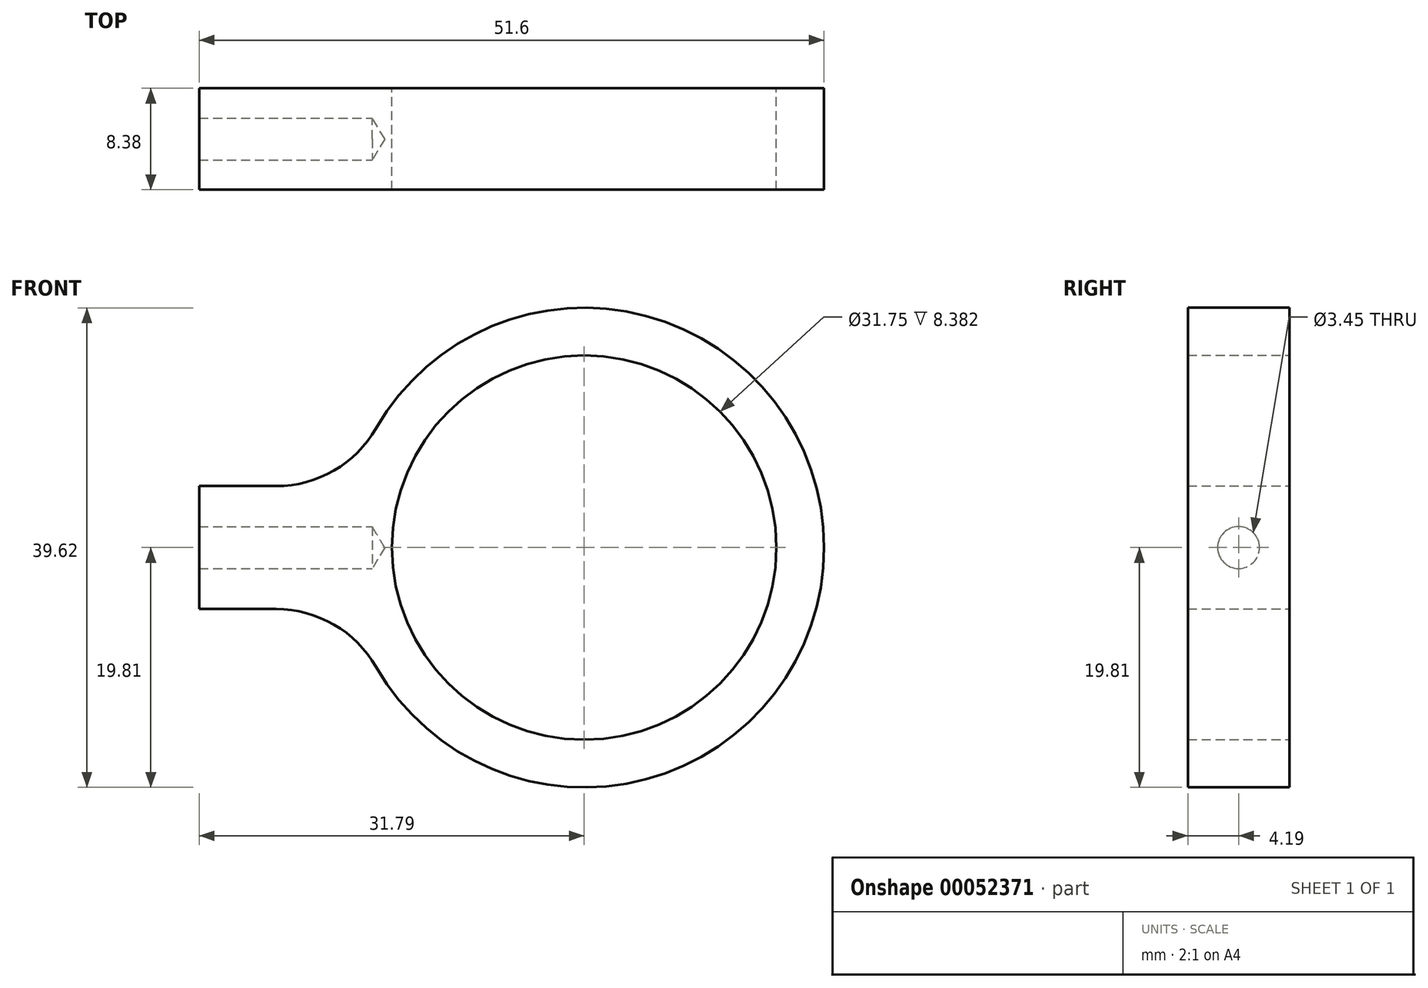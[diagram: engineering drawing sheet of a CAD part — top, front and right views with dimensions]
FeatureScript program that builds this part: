
annotation { "Feature Type Name" : "Feature", "Feature Type Description" : "" }
export const myFeature = defineFeature(function(context is Context, id is Id, definition is map)
    precondition{}
    {
        {
            var Q0;
            Q0=qCreatedBy(makeId("Front.planeOp"),FACE);
            var sketch = newSketch(context, id + "F0", { "sketchPlane" : qUnion([Q0])});
            skCircle(sketch, "E0", {"center": v(0, 0) * mm, "radius": 15.88 * mm});
            skArc(sketch, "E1", {"start": v(-17.18, 9.86) * mm, "mid": v(19.81, 0) * mm, "end": v(-17.18, -9.86) * mm});
            skLineSegment(sketch, "E2", {"start": v(-25.44, -5.08) * mm, "end": v(-31.8, -5.08) * mm});
            skLineSegment(sketch, "E3", {"start": v(-31.8, -5.08) * mm, "end": v(-31.8, 5.08) * mm});
            skLineSegment(sketch, "E4", {"start": v(-31.8, 5.08) * mm, "end": v(-25.44, 5.08) * mm});
            skPoint(sketch, "E5", {"position": v(-31.8, 0) * mm});
            skPoint(sketch, "E6.visualSharp", {"position": v(-19.15, 5.08) * mm});
            skArc(sketch, "E6.filletArc", {"start": v(-25.44, 5.08) * mm, "mid": v(-20.67, 6.36) * mm, "end": v(-17.18, 9.86) * mm});
            skPoint(sketch, "E7.visualSharp", {"position": v(-19.15, -5.08) * mm});
            skArc(sketch, "E7.filletArc", {"start": v(-17.18, -9.86) * mm, "mid": v(-20.67, -6.36) * mm, "end": v(-25.44, -5.08) * mm});
            skSolve(sketch);
        }
        {
            var Q0;
            Q0 = qSketchRegion(id + "F0", true);
            extrude(context, id + "F1", {"entities" : qUnion([Q0]), "depth" : 8.38 * mm, "symmetric" : true});
        }
        {
            var Q0;
            Q0=makeQuery(id+"F1.opExtrude","SWEPT_FACE",FACE,{"disambiguationData":[OSD([sQuery(id+"F0.wireOp",EDGE,"E3")])]});
            var sketch = newSketch(context, id + "F2", { "sketchPlane" : qUnion([Q0])});
            skPoint(sketch, "E8", {"position": v(0, 0) * mm});
            skSolve(sketch);
        }
        {
            var Q0;
            Q0=sQuery(id+"F2.wireOp",VERTEX,"E8");
            var Q1;
            Q1=makeQuery(id+"F1.opExtrude","SWEPT_BODY",BODY,{"disambiguationData":[OSD([sQuery(id+"F0.wireOp",EDGE,"E0"),sQuery(id+"F0.wireOp",EDGE,"E1"),sQuery(id+"F0.wireOp",EDGE,"E2"),sQuery(id+"F0.wireOp",EDGE,"E3"),sQuery(id+"F0.wireOp",EDGE,"E4"),sQuery(id+"F0.wireOp",EDGE,"E6.filletArc"),sQuery(id+"F0.wireOp",EDGE,"E7.filletArc")])]});
            hole(context, id + "F3", {"style" : HoleStyle.SIMPLE, "holeDiameter" : 3.45 * mm, "endStyle" : HoleEndStyle.BLIND, "holeDepth" : 14.29 * mm, "locations" : qUnion([Q0]), "scope" : qUnion([Q1])});
        }
    });
